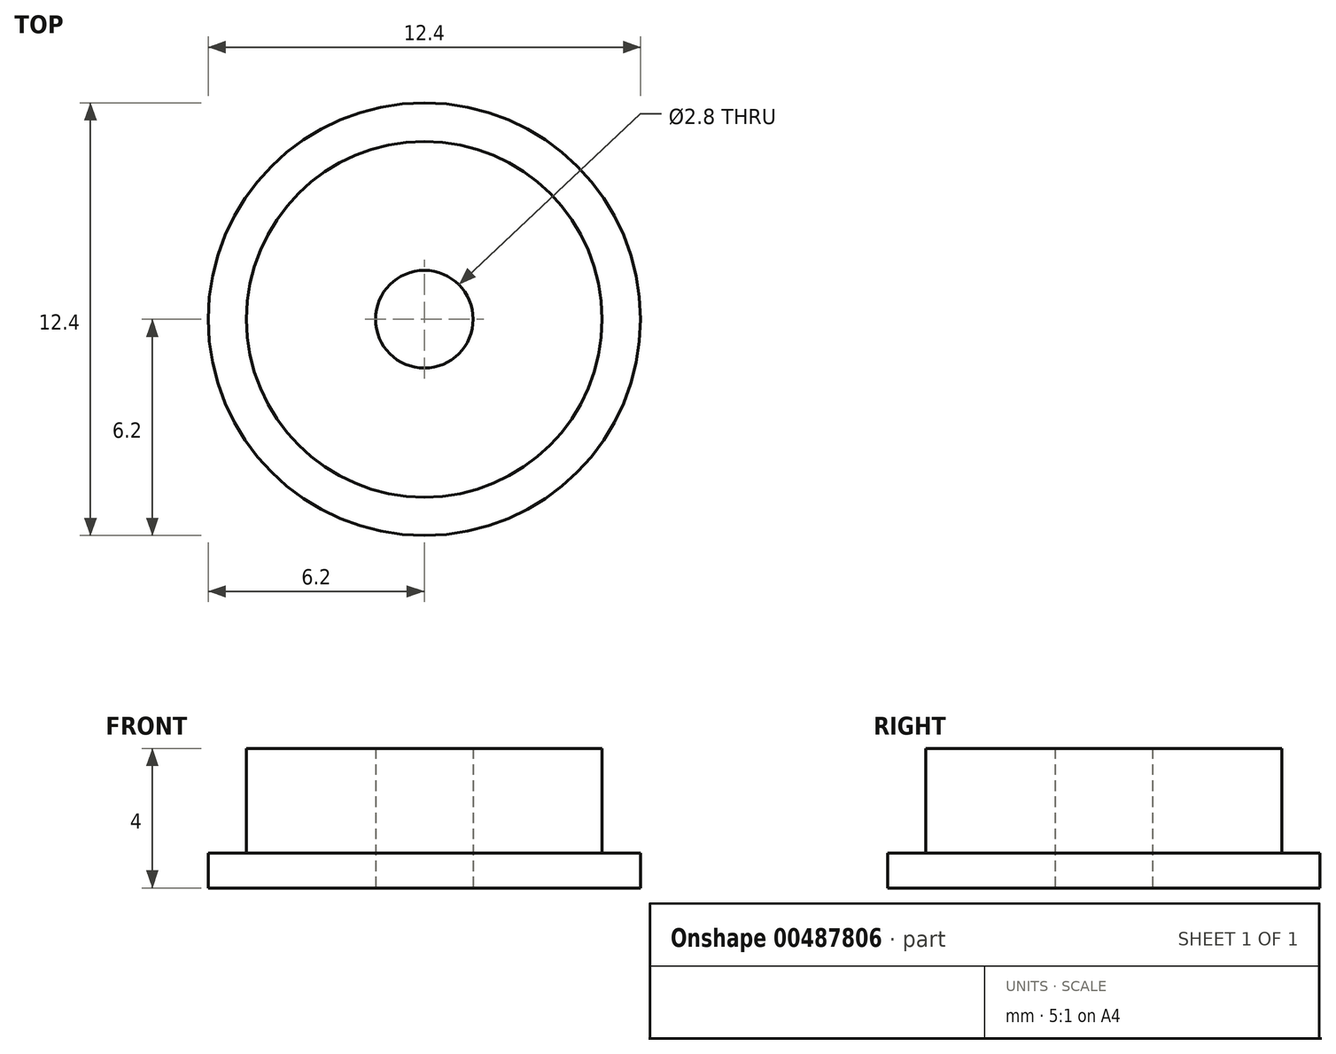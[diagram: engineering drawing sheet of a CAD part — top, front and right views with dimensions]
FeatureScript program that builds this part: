
annotation { "Feature Type Name" : "Feature", "Feature Type Description" : "" }
export const myFeature = defineFeature(function(context is Context, id is Id, definition is map)
    precondition{}
    {
        {
            var Q0;
            Q0=qCreatedBy(makeId("Front.planeOp"),FACE);
            var sketch = newSketch(context, id + "F0", { "sketchPlane" : qUnion([Q0])});
            skLineSegment(sketch, "E0", {"start": v(1.4, 0) * mm, "end": v(1.4, 4) * mm});
            skLineSegment(sketch, "E1", {"start": v(1.4, 4) * mm, "end": v(5.1, 4) * mm});
            skLineSegment(sketch, "E2", {"start": v(1.4, 0) * mm, "end": v(6.2, 0) * mm});
            skLineSegment(sketch, "E3", {"start": v(6.2, 0) * mm, "end": v(6.2, 1) * mm});
            skLineSegment(sketch, "E4", {"start": v(6.2, 1) * mm, "end": v(5.1, 1) * mm});
            skLineSegment(sketch, "E5", {"start": v(5.1, 1) * mm, "end": v(5.1, 4) * mm});
            skLineSegment(sketch, "E6", {"start": v(0, 0) * mm, "end": v(0, 5.12) * mm, "construction": true});
            skSolve(sketch);
        }
        {
            var Q0;
            Q0=makeQuery(id+"F0.imprint","IMPRINT",FACE,{"disambiguationData":[TD([[makeQuery(id+"F0.imprint","IMPRINT",EDGE,{"derivedFrom":sQuery(id+"F0.wireOp",EDGE,"E0")}),-1.0]])]});
            var Q1;
            Q1=sQuery(id+"F0.wireOp",EDGE,"E6");
            revolve(context, id + "F1", {"entities" : qUnion([Q0]), "axis" : qUnion([Q1]), "revolveType" : RevolveType.FULL});
        }
    });
